# Revit family: V-LENSESxx150xxSWxx
name_source: partatom
category: Leuchten
units: mm (PartAtom-declared; Revit-internal decimal feet)

## family parameters
Basisbauteil = Fläche
Beim Laden mit Abzugskörper schneiden = Nein
Bemaßung runder Anschluss = Durchmesser verwenden
Gemeinsam genutzt = Nein
Lichtquelle = Ja
OmniClass-Nummer = 23.80.70.11
OmniClass-Titel = Luminaries for Internal Lighting
Raumberechnungspunkt = Nein
Teiletyp = Normal

## types (4) — shared parameters
Baugruppenkennzeichen = D5020200
Emissionsform beim Rendern sichtbar = Nein
Farbfilter = 16777215
Farbtemperaturverschiebung bei Dämpfen der Lampe = <Keine Auswahl>
Hersteller = RIDI Leuchten GmbH
Lampe = LED
Neigungswinkel = 90.00°
URL = www.ridi.de
Von Breite des Rechtecks ausssenden = 1272 mm  [stored 4.17323 ft]
Von Länge des Rechtecks aussenden = 111 mm
brand = RIDI
conformity mark = CE
electrical safety class = 1
height = 83 mm  [stored 0.27231 ft]
ingress protection (IP) code = IP20
length = 1500 mm  [stored 4.92126 ft]
nominal frequency = 50-60Hz
nominal voltage = 230
voltage type (AC, DC, UC) = AC
width = 113 mm  [stored 0.370735 ft]
zero-valued in all types: Vorgabe-Ansicht

## per-type parameters (varying)
| type | Datei für fotometrisches Netz | Modell | Scheinlast | product name | rated input power | weight |
| V-LENSES-D150-5RFSW840B0550 | V-LENSES-D.IES | 1522576SW | 32 VA | V-LENSES-D150-5RFSW840B0550
V-LENSES-D150-5RFSW840B0550 | 32 | 3,3 |
| V-LENSES-D150-7DASW840B0500 | V-LENSES-D.IES | 1532575SW | 33 VA | V-LENSES-D150-7DASW840B0500
V-LENSES-D150-5RFSW840B0550 | 33 | 3,3 |
| V-LENSES-DI150-7DASW840B0700 | V-LENSES-DI.IES | 1532577SW | 47 VA | V-LENSES-DI150-7DASW840B0700
V-LENSES-D150-5RFSW840B0550 | 47 | 3,6 |
| V-LENSES-DI150-5RFSW840B0700 | V-LENSES-DI.IES | 1522578SW | 47 VA | V-LENSES-DI150-5RFSW840B0700
V-LENSES-D150-5RFSW840B0550 | 47 | 3,6 |

note: [stored X ft] marks values corroborated as IEEE doubles in the binary element streams (Revit-internal decimal feet)
